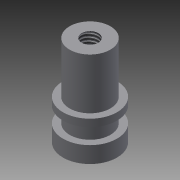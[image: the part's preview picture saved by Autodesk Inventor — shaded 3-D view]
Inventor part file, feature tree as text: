
AUTODESK INVENTOR PART (.ipt)
format: ipt  version: 2014 (Build 180170000, 170)  size: 101,376 bytes
history: native  units: mm
features: sketch x5, extrude x4, hole x1
ambient origin geometry x8: Origin, YZ Plane, XZ Plane, XY Plane, X Axis, Y Axis, Z Axis, Center Point
bodies: Solid1 (feature_tree)
feature tree (10):
  extrude  "Extrusion1"  Depth=4.82mm TaperAngle=0.0deg
  extrude  "Extrusion2"  Depth=4.6mm TaperAngle=0.0deg
  extrude  "Extrusion3"  Depth=2.15mm
  extrude  "Extrusion4"  [1 undecoded]
  hole  "Hole1"  [1 undecoded]
  sketch  "Sketch1"  dims[d0=15.9mm d1=4.82mm d2=0.0mm]
  sketch  "Sketch2"  dims[d3=12.0mm d4=4.6mm d5=0.0mm]
  sketch  "Sketch3"  dims[d6=2.15mm d7=0.0mm d8=12.0mm]
  sketch  "Sketch4"  dims[d9=15.0mm d10=0.0mm]
  sketch  "Sketch5"  dims[d11=4.917mm d12=6.0mm d13=4.0mm d14=2.0mm d15=90.0deg d16=8.0mm d17=20.594885mm]
note: 2 required parameter values undecoded (feature->parameter linkage not recoverable at this tier; creation-order binding heuristic only, values carry confidence <= 0.55)
